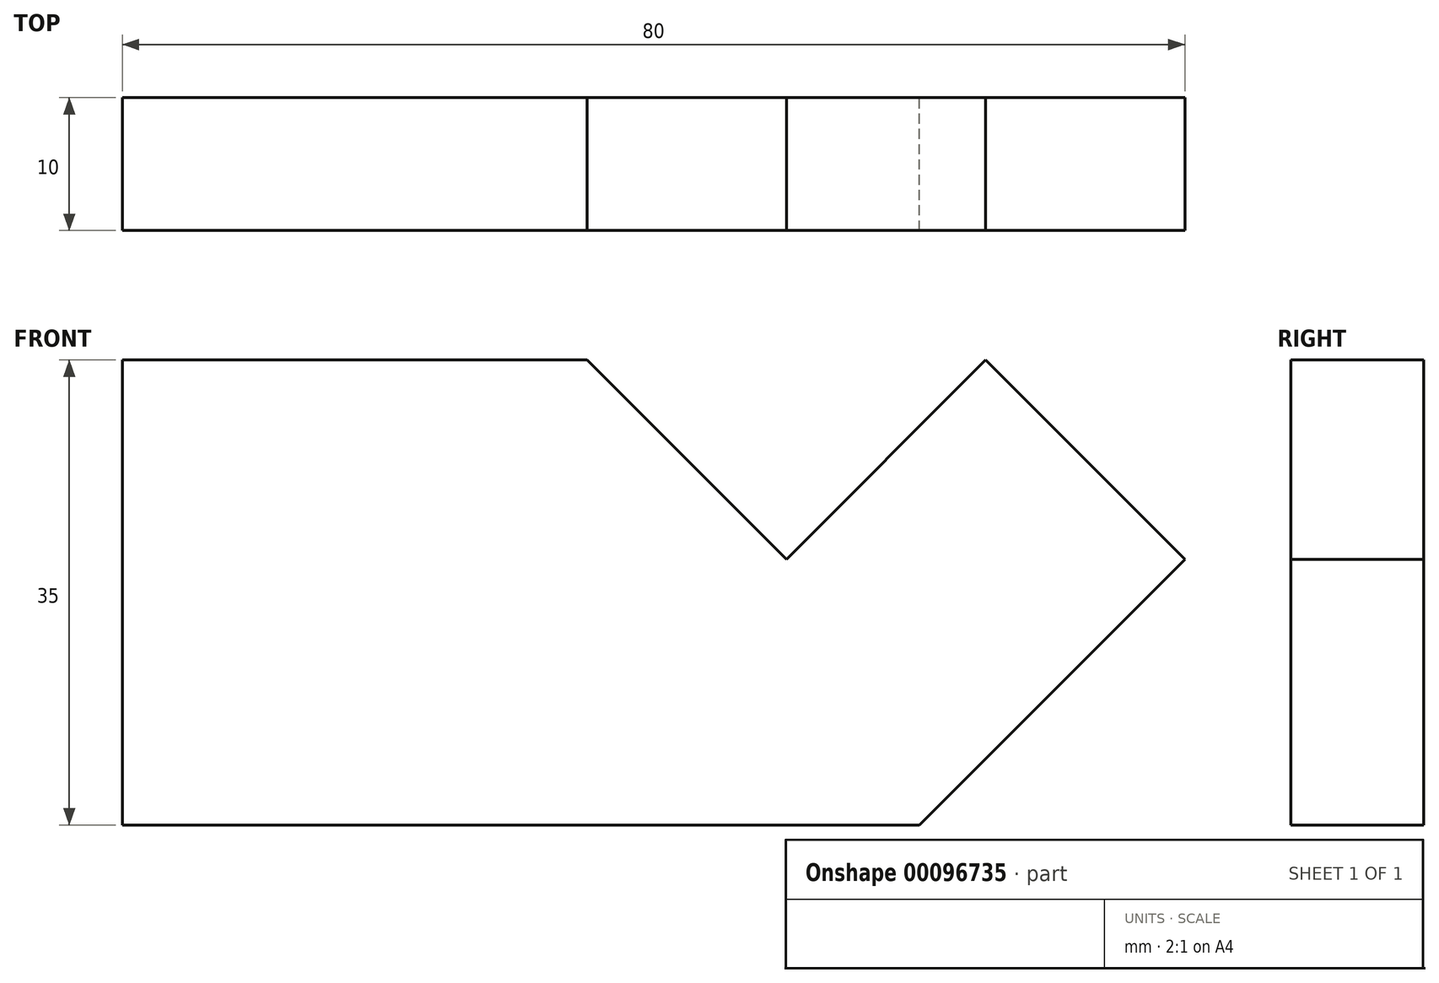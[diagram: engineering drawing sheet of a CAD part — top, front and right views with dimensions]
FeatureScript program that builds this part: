
annotation { "Feature Type Name" : "Feature", "Feature Type Description" : "" }
export const myFeature = defineFeature(function(context is Context, id is Id, definition is map)
    precondition{}
    {
        {
            var Q0;
            Q0=qCreatedBy(makeId("Front.planeOp"),FACE);
            var sketch = newSketch(context, id + "F0", { "sketchPlane" : qUnion([Q0])});
            skLineSegment(sketch, "E0", {"start": v(0, 0) * mm, "end": v(60, 0) * mm});
            skLineSegment(sketch, "E1", {"start": v(60, 0) * mm, "end": v(80, 20) * mm});
            skLineSegment(sketch, "E2", {"start": v(80, 20) * mm, "end": v(65, 35) * mm});
            skLineSegment(sketch, "E3", {"start": v(65, 35) * mm, "end": v(35, 35) * mm, "construction": true});
            skLineSegment(sketch, "E4", {"start": v(35, 35) * mm, "end": v(0, 35) * mm});
            skLineSegment(sketch, "E5", {"start": v(0, 35) * mm, "end": v(0, 0) * mm});
            skLineSegment(sketch, "E6", {"start": v(35, 35) * mm, "end": v(50, 20) * mm});
            skLineSegment(sketch, "E7", {"start": v(50, 20) * mm, "end": v(65, 35) * mm});
            skSolve(sketch);
        }
        {
            var Q0;
            Q0=makeQuery(id+"F0.imprint","IMPRINT",FACE,{"disambiguationData":[TD([[makeQuery(id+"F0.imprint","IMPRINT",EDGE,{"derivedFrom":sQuery(id+"F0.wireOp",EDGE,"E0")}),1.0]])]});
            extrude(context, id + "F1", {"entities" : qUnion([Q0]), "depth" : 10 * mm});
        }
    });
